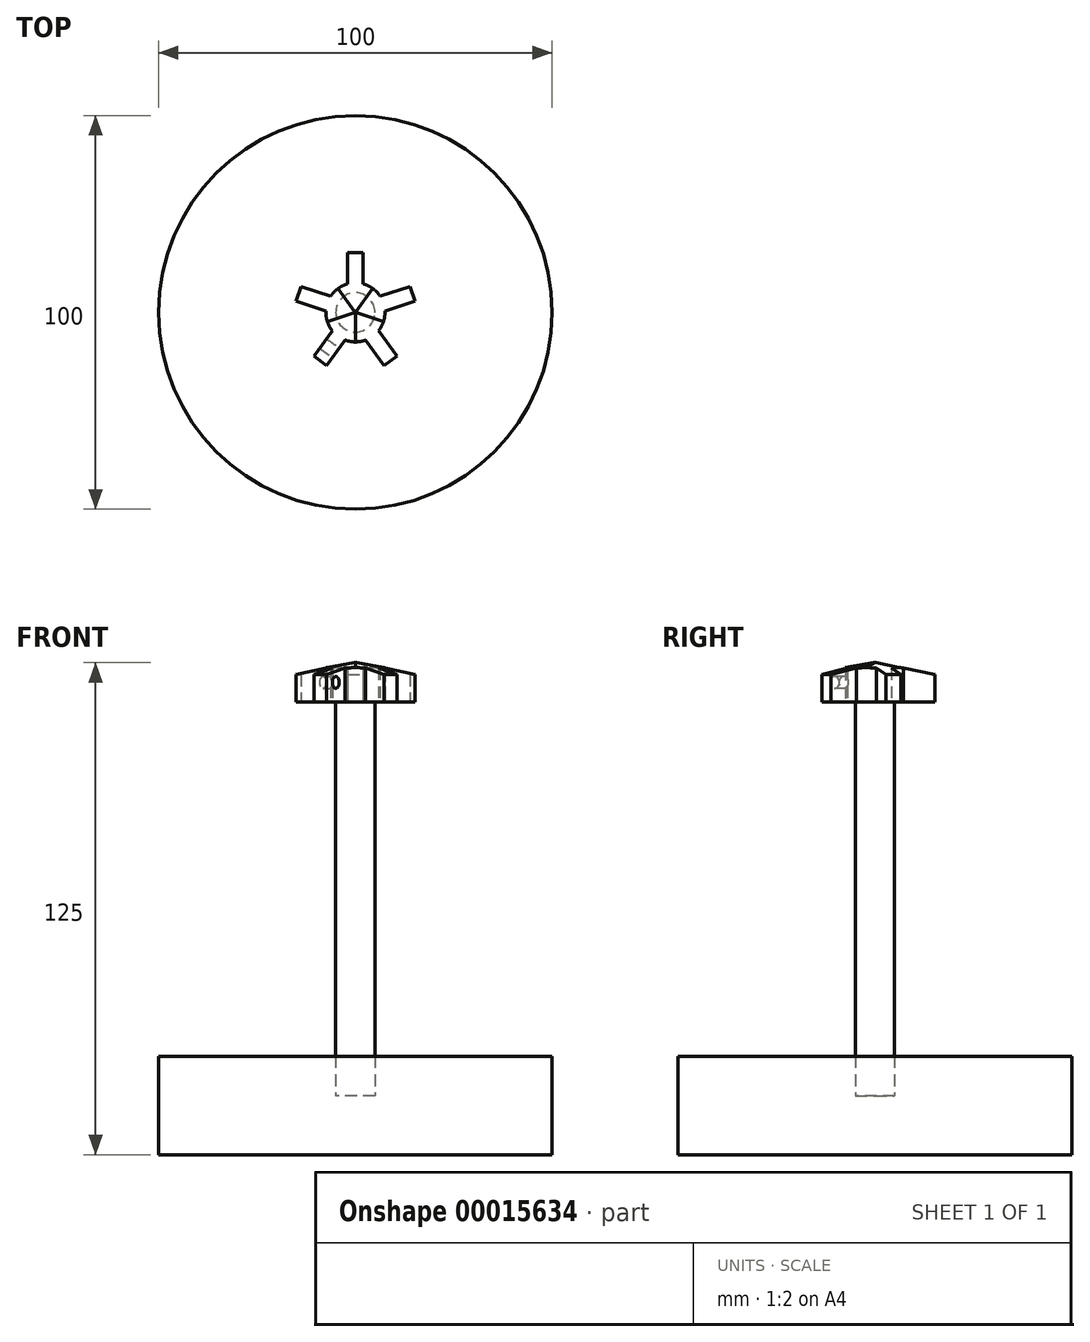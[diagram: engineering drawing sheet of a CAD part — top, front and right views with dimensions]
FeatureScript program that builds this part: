
annotation { "Feature Type Name" : "Feature", "Feature Type Description" : "" }
export const myFeature = defineFeature(function(context is Context, id is Id, definition is map)
    precondition{}
    {
        {
            var Q0;
            Q0=qCreatedBy(makeId("Top.planeOp"),FACE);
            var sketch = newSketch(context, id + "F0", { "sketchPlane" : qUnion([Q0])});
            skCircle(sketch, "E0", {"center": v(0, 0) * mm, "radius": 50 * mm});
            skSolve(sketch);
        }
        {
            var Q0;
            Q0=makeQuery(id+"F0.imprint","IMPRINT",FACE,{"disambiguationData":[TD([[makeQuery(id+"F0.imprint","IMPRINT",EDGE,{"derivedFrom":sQuery(id+"F0.wireOp",EDGE,"E0")}),1.0]])]});
            extrude(context, id + "F1", {"entities" : qUnion([Q0]), "depth" : 25 * mm});
        }
        {
            var Q0;
            Q0=makeQuery(id+"F1.opExtrude","CAP_FACE",FACE,{"disambiguationData":[OSD([sQuery(id+"F0.wireOp",EDGE,"E0")])],"isStart":false});
            var sketch = newSketch(context, id + "F2", { "sketchPlane" : qUnion([Q0])});
            skCircle(sketch, "E1", {"center": v(0, 0) * mm, "radius": 5 * mm});
            skSolve(sketch);
        }
        {
            var Q0;
            Q0=makeQuery(id+"F2.imprint","IMPRINT",FACE,{"disambiguationData":[TD([[makeQuery(id+"F2.imprint","IMPRINT",EDGE,{"derivedFrom":sQuery(id+"F2.wireOp",EDGE,"E1")}),1.0]])]});
            extrude(context, id + "F3", {"entities" : qUnion([Q0]), "operationType" : NewBodyOperationType.REMOVE, "oppositeDirection" : true, "depth" : 10 * mm});
        }
        {
            var Q0;
            Q0=makeQuery(id+"F3.boolean.opBoolean","COPY",FACE,{"derivedFrom":makeQuery(id+"F3.opExtrude","CAP_FACE",FACE,{"disambiguationData":[OSD([sQuery(id+"F2.wireOp",EDGE,"E1")])],"isStart":false})});
            var sketch = newSketch(context, id + "F4", { "sketchPlane" : qUnion([Q0])});
            skCircle(sketch, "E2", {"center": v(0, 0) * mm, "radius": 5 * mm});
            skSolve(sketch);
        }
        {
            var Q0;
            Q0 = qSketchRegion(id + "F4", true);
            extrude(context, id + "F5", {"entities" : qUnion([Q0]), "depth" : 100 * mm});
        }
        {
            var Q0;
            Q0=makeQuery(id+"F5.opExtrude","CAP_FACE",FACE,{"disambiguationData":[OSD([sQuery(id+"F4.wireOp",EDGE,"E2")])],"isStart":false});
            var sketch = newSketch(context, id + "F6", { "sketchPlane" : qUnion([Q0])});
            skCircle(sketch, "E3", {"center": v(0, 0) * mm, "radius": 7.5 * mm});
            skLineSegment(sketch, "E4.bottom", {"start": v(-2, 7.23) * mm, "end": v(2, 7.23) * mm});
            skLineSegment(sketch, "E4.top", {"start": v(-2, 15.23) * mm, "end": v(2, 15.23) * mm});
            skLineSegment(sketch, "E4.left", {"start": v(-2, 7.23) * mm, "end": v(-2, 15.23) * mm});
            skLineSegment(sketch, "E4.right", {"start": v(2, 7.23) * mm, "end": v(2, 15.23) * mm});
            skLineSegment(sketch, "E5", {"start": v(0, 17.32) * mm, "end": v(0, 0) * mm, "construction": true});
            skLineSegment(sketch, "E6.1.0", {"start": v(-7.5, 0.33) * mm, "end": v(-6.26, 4.14) * mm});
            skLineSegment(sketch, "E6.1.1", {"start": v(-7.5, 0.33) * mm, "end": v(-15.1, 2.8) * mm});
            skLineSegment(sketch, "E6.1.2", {"start": v(-15.1, 2.8) * mm, "end": v(-13.87, 6.6) * mm});
            skLineSegment(sketch, "E6.1.3", {"start": v(-6.26, 4.14) * mm, "end": v(-13.87, 6.6) * mm});
            skLineSegment(sketch, "E6.2.0", {"start": v(-2.63, -7.02) * mm, "end": v(-5.87, -4.67) * mm});
            skLineSegment(sketch, "E6.2.1", {"start": v(-2.63, -7.02) * mm, "end": v(-7.33, -13.5) * mm});
            skLineSegment(sketch, "E6.2.2", {"start": v(-7.33, -13.5) * mm, "end": v(-10.57, -11.14) * mm});
            skLineSegment(sketch, "E6.2.3", {"start": v(-5.87, -4.67) * mm, "end": v(-10.57, -11.14) * mm});
            skLineSegment(sketch, "E6.3.0", {"start": v(5.87, -4.67) * mm, "end": v(2.63, -7.02) * mm});
            skLineSegment(sketch, "E6.3.1", {"start": v(5.87, -4.67) * mm, "end": v(10.57, -11.14) * mm});
            skLineSegment(sketch, "E6.3.2", {"start": v(10.57, -11.14) * mm, "end": v(7.33, -13.5) * mm});
            skLineSegment(sketch, "E6.3.3", {"start": v(2.63, -7.02) * mm, "end": v(7.33, -13.5) * mm});
            skLineSegment(sketch, "E6.4.0", {"start": v(6.26, 4.14) * mm, "end": v(7.5, 0.33) * mm});
            skLineSegment(sketch, "E6.4.1", {"start": v(6.26, 4.14) * mm, "end": v(13.87, 6.6) * mm});
            skLineSegment(sketch, "E6.4.2", {"start": v(13.87, 6.6) * mm, "end": v(15.1, 2.8) * mm});
            skLineSegment(sketch, "E6.4.3", {"start": v(7.5, 0.33) * mm, "end": v(15.1, 2.8) * mm});
            skSolve(sketch);
        }
        {
            var Q0;
            Q0 = qSketchRegion(id + "F6", true);
            extrude(context, id + "F7", {"entities" : qUnion([Q0]), "operationType" : NewBodyOperationType.ADD, "depth" : 10 * mm});
        }
        {
            var Q0;
            Q0=makeQuery(id+"F7.opExtrude","SWEPT_FACE",FACE,{"disambiguationData":[OSD([sQuery(id+"F6.wireOp",EDGE,"E6.2.1")])]});
            var sketch = newSketch(context, id + "F8", { "sketchPlane" : qUnion([Q0])});
            skCircle(sketch, "E7", {"center": v(-11.23, 120) * mm, "radius": 1.5 * mm});
            skLineSegment(sketch, "E8", {"start": v(-15.23, 120) * mm, "end": v(-7.23, 120) * mm, "construction": true});
            skLineSegment(sketch, "E9", {"start": v(-11.23, 125) * mm, "end": v(-11.23, 115) * mm, "construction": true});
            skSolve(sketch);
        }
        {
            var Q0;
            Q0 = qSketchRegion(id + "F8", true);
            extrude(context, id + "F9", {"entities" : qUnion([Q0]), "operationType" : NewBodyOperationType.REMOVE, "endBound" : BoundingType.THROUGH_ALL, "oppositeDirection" : true, "depth" : 25 * mm});
        }
        {
            var Q0;
            Q0=makeQuery(id+"F7.opExtrude","CAP_EDGE",EDGE,{"disambiguationData":[OSD([sQuery(id+"F6.wireOp",EDGE,"E6.2.2")])],"isStart":false});
            var Q1;
            Q1=makeQuery(id+"F7.opExtrude","CAP_EDGE",EDGE,{"disambiguationData":[OSD([sQuery(id+"F6.wireOp",EDGE,"E6.3.2")])],"isStart":false});
            var Q2;
            Q2=makeQuery(id+"F7.opExtrude","CAP_EDGE",EDGE,{"disambiguationData":[OSD([sQuery(id+"F6.wireOp",EDGE,"E6.4.2")])],"isStart":false});
            var Q3;
            Q3=makeQuery(id+"F7.opExtrude","CAP_EDGE",EDGE,{"disambiguationData":[OSD([sQuery(id+"F6.wireOp",EDGE,"E4.top")])],"isStart":false});
            var Q4;
            Q4=makeQuery(id+"F7.opExtrude","CAP_EDGE",EDGE,{"disambiguationData":[OSD([sQuery(id+"F6.wireOp",EDGE,"E6.1.2")])],"isStart":false});
            chamfer(context, id + "F10", {"entities" : qUnion([Q0, Q1, Q2, Q3, Q4]), "chamferType" : ChamferType.TWO_OFFSETS, "width1" : 3 * mm, "oppositeDirection" : false, "width2" : 15 * mm, "tangentPropagation" : true});
        }
    });
